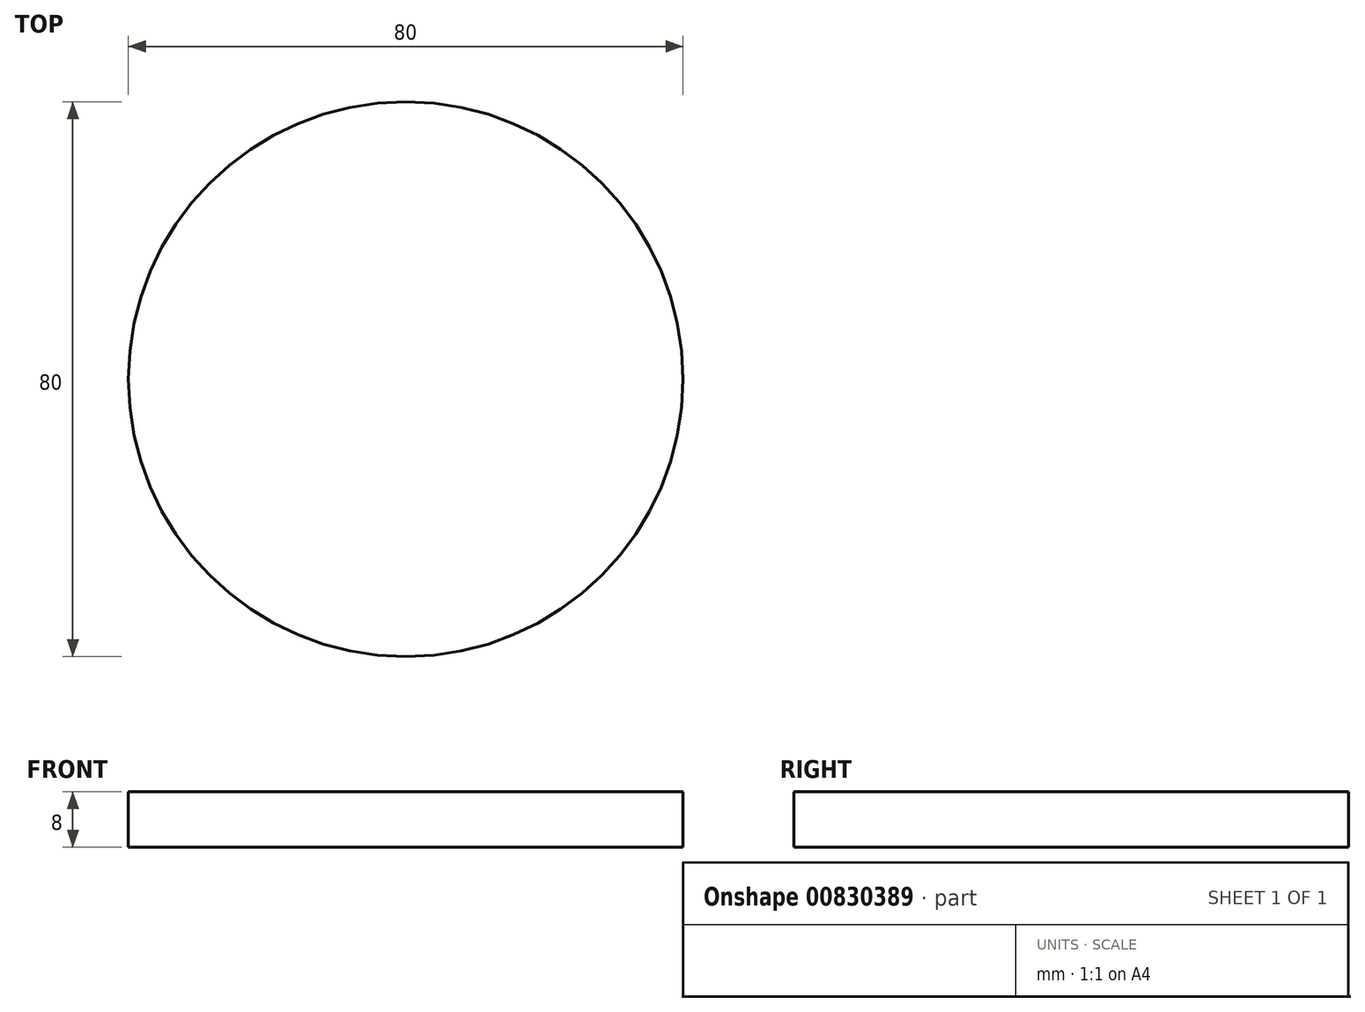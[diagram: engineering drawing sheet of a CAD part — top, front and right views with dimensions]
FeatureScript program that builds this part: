
annotation { "Feature Type Name" : "Feature", "Feature Type Description" : "" }
export const myFeature = defineFeature(function(context is Context, id is Id, definition is map)
    precondition{}
    {
        {
            var Q0;
            Q0=qCreatedBy(makeId("Top.planeOp"),FACE);
            var sketch = newSketch(context, id + "F0", { "sketchPlane" : qUnion([Q0])});
            skCircle(sketch, "E0", {"center": v(0, 0) * mm, "radius": 40 * mm});
            skSolve(sketch);
        }
        {
            var Q0;
            Q0 = qSketchRegion(id + "F0", true);
            extrude(context, id + "F1", {"entities" : qUnion([Q0]), "depth" : 8 * mm, "offsetDistance" : 25 * mm});
        }
    });
